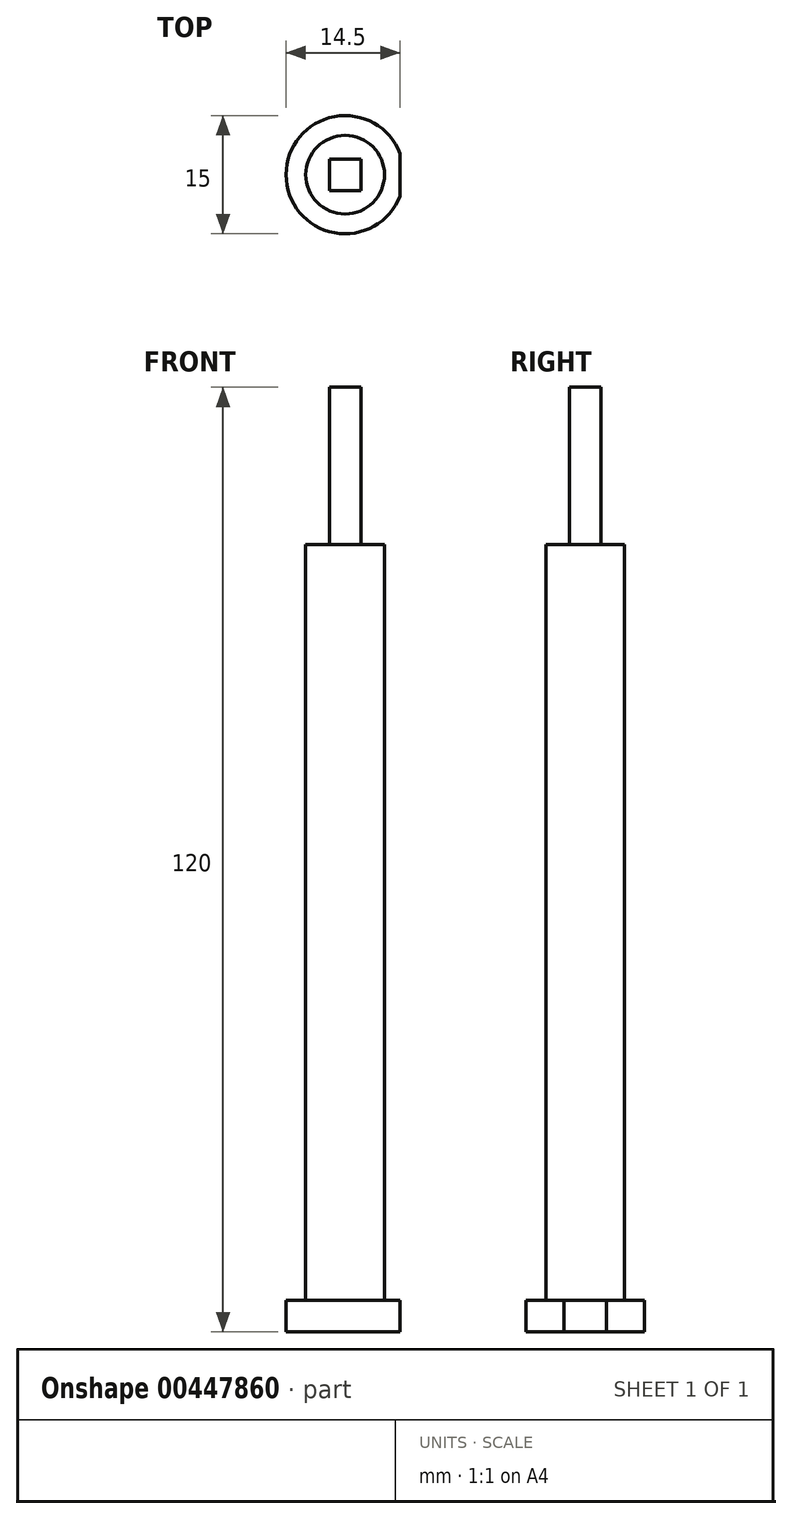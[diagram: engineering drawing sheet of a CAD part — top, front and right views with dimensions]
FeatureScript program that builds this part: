
annotation { "Feature Type Name" : "Feature", "Feature Type Description" : "" }
export const myFeature = defineFeature(function(context is Context, id is Id, definition is map)
    precondition{}
    {
        {
            var Q0;
            Q0=qCreatedBy(makeId("Top.planeOp"),FACE);
            var sketch = newSketch(context, id + "F0", { "sketchPlane" : qUnion([Q0])});
            skCircle(sketch, "E0", {"center": v(0, 0) * mm, "radius": 7.5 * mm});
            skSolve(sketch);
        }
        {
            var Q0;
            Q0=qSketchRegion(id+"F0",true);
            extrude(context, id + "F1", {"entities" : qUnion([Q0]), "depth" : 4 * mm});
        }
        {
            var Q0;
            Q0=qCreatedBy(makeId("Top.planeOp"),FACE);
            var sketch = newSketch(context, id + "F2", { "sketchPlane" : qUnion([Q0])});
            skCircle(sketch, "E1", {"center": v(0, 0) * mm, "radius": 5 * mm});
            skSolve(sketch);
        }
        {
            var Q0;
            Q0=qSketchRegion(id+"F2",true);
            extrude(context, id + "F3", {"entities" : qUnion([Q0]), "operationType" : NewBodyOperationType.ADD, "depth" : 100 * mm});
        }
        {
            var Q0;
            Q0=makeQuery(id+"F3.opExtrude","CAP_FACE",FACE,{"disambiguationData":[OSD([sQuery(id+"F2.wireOp",EDGE,"E1")])],"isStart":false});
            var sketch = newSketch(context, id + "F4", { "sketchPlane" : qUnion([Q0])});
            skLineSegment(sketch, "E2.bottom", {"start": v(-2, 2) * mm, "end": v(2, 2) * mm});
            skLineSegment(sketch, "E2.top", {"start": v(-2, -2) * mm, "end": v(2, -2) * mm});
            skLineSegment(sketch, "E2.left", {"start": v(-2, 2) * mm, "end": v(-2, -2) * mm});
            skLineSegment(sketch, "E2.right", {"start": v(2, 2) * mm, "end": v(2, -2) * mm});
            skSolve(sketch);
        }
        {
            var Q0;
            Q0=makeQuery(id+"F4.imprint","IMPRINT",FACE,{"disambiguationData":[TD([[makeQuery(id+"F4.imprint","IMPRINT",EDGE,{"derivedFrom":sQuery(id+"F4.wireOp",EDGE,"E2.bottom")}),-1.0]])]});
            extrude(context, id + "F5", {"entities" : qUnion([Q0]), "operationType" : NewBodyOperationType.ADD, "depth" : 20 * mm});
        }
        {
            var Q0;
            Q0=qCreatedBy(makeId("Top.planeOp"),FACE);
            var sketch = newSketch(context, id + "F6", { "sketchPlane" : qUnion([Q0])});
            skLineSegment(sketch, "E3.bottom", {"start": v(7, -16.3) * mm, "end": v(17.3, -16.3) * mm});
            skLineSegment(sketch, "E3.top", {"start": v(7, 16.58) * mm, "end": v(17.3, 16.58) * mm});
            skLineSegment(sketch, "E3.left", {"start": v(7, -16.3) * mm, "end": v(7, 16.58) * mm});
            skLineSegment(sketch, "E3.right", {"start": v(17.3, -16.3) * mm, "end": v(17.3, 16.58) * mm});
            skSolve(sketch);
        }
        {
            var Q0;
            Q0=makeQuery(id+"F6.imprint","IMPRINT",FACE,{"disambiguationData":[TD([[makeQuery(id+"F6.imprint","IMPRINT",EDGE,{"derivedFrom":sQuery(id+"F6.wireOp",EDGE,"E3.bottom")}),1.0]])]});
            extrude(context, id + "F7", {"entities" : qUnion([Q0]), "operationType" : NewBodyOperationType.REMOVE, "depth" : 25 * mm});
        }
    });
